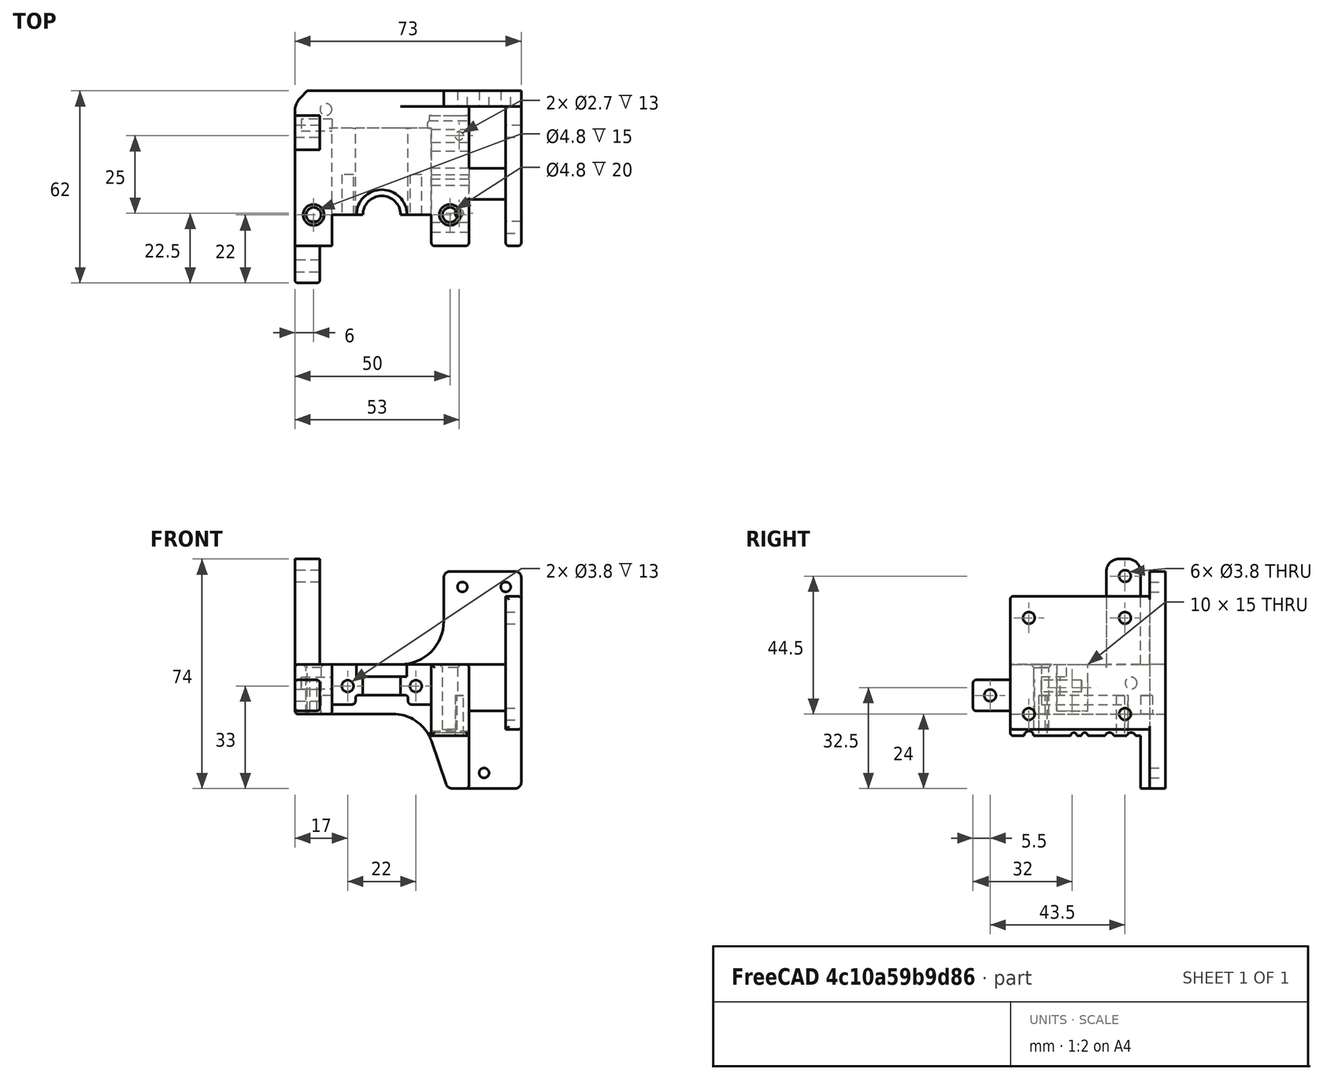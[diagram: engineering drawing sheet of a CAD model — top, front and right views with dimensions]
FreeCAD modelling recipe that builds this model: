
FCSTD DOCUMENT  (FreeCAD 0.19R)
Label: head7.1
License: All rights reserved
LicenseURL: http://en.wikipedia.org/wiki/All_rights_reserved
objects: Sketcher::SketchObject×22, PartDesign::Pocket×19, PartDesign::Fillet×15, PartDesign::Pad×3, PartDesign::Chamfer×2, PartDesign::Body×1, Mesh::Feature×1
note: 101 computed .brp shape members not serialized (recipe doc carries the construction recipe); baked Part::Feature solids carry a one-line shape summary decoded from their .brp

FEATURE [Sketcher::SketchObject] Sketch
  FullyConstrained = true
  MapMode = 5
  Support = -> [XY_Plane]
  sketch-geometry (5):
    g0: LineSegment StartX=0 StartY=0 StartZ=0 EndX=45 EndY=0 EndZ=0
    g1: LineSegment StartX=-28 StartY=0 StartZ=0 EndX=0 EndY=0 EndZ=0
    g2: LineSegment StartX=-28 StartY=0 StartZ=0 EndX=-28 EndY=-50 EndZ=0
    g3: LineSegment StartX=-28 StartY=-50 StartZ=0 EndX=45 EndY=-50 EndZ=0
    g4: LineSegment StartX=45 StartY=-50 StartZ=0 EndX=45 EndY=0 EndZ=0
  constraints (14):
    c: Coincident(g-1,g0)
    c: PointOnObject(g0,g-1)
    c: PointOnObject(g1,g-1)
    c: Coincident(g1,g0)
    c: Coincident(g1,g2)
    c: Vertical(g2)
    c: Coincident(g2,g3)
    c: Horizontal(g3)
    c: Coincident(g3,g4)
    c: Coincident(g4,g0)
    c: Vertical(g4)
    c: Distance(g4) = 50
    c: DistanceX(g0) = 45
    c: DistanceX(g1) = -28
FEATURE [PartDesign::Pad] Pad
  Direction = (1,1,1)
  Length = 70
  Length2 = 100
  Profile = -> Sketch
  Type = 0
FEATURE [Sketcher::SketchObject] Sketch001
  FullyConstrained = false
  MapMode = 5
  Placement = pos=(0,0,70) rot=(0,0,1;0rad)
  Support = -> [Pad]
  sketch-geometry (4):
    g0: LineSegment StartX=28.1122 StartY=-5 StartZ=0 EndX=40 EndY=-5 EndZ=0
    g1: LineSegment StartX=40 StartY=-5 StartZ=0 EndX=40 EndY=-51.78 EndZ=0
    g2: LineSegment StartX=40 StartY=-51.78 StartZ=0 EndX=28.1122 EndY=-51.78 EndZ=0
    g3: LineSegment StartX=28.1122 StartY=-51.78 StartZ=0 EndX=28.1122 EndY=-5 EndZ=0
  constraints (11):
    c: Coincident(g0,g1)
    c: Coincident(g1,g2)
    c: Coincident(g2,g3)
    c: Coincident(g3,g0)
    c: Horizontal(g0)
    c: Horizontal(g2)
    c: Vertical(g1)
    c: Vertical(g3)
    c: DistanceX(g0) = 40
    c: DistanceY(g1) = -51.78
    c: DistanceY(g0) = -5
FEATURE [PartDesign::Pocket] Pocket  label="BOBnotch"
  BaseFeature = -> Pad
  Length = 5
  Length2 = 100
  Profile = -> Sketch001
  Type = 1
FEATURE [Sketcher::SketchObject] Sketch002
  FullyConstrained = false
  MapMode = 5
  Placement = pos=(0,0,70) rot=(0,0,1;0rad)
  Support = -> [Pocket]
  sketch-geometry (6):
    g0: LineSegment StartX=30 StartY=-5 StartZ=0 EndX=30 EndY=-65.096 EndZ=0
    g1: LineSegment StartX=30 StartY=-65.096 StartZ=0 EndX=-40.7834 EndY=-65.096 EndZ=0
    g2: LineSegment StartX=-40.7834 StartY=-65.096 StartZ=0 EndX=-40.7834 EndY=12.9948 EndZ=0
    g3: LineSegment StartX=-40.7834 StartY=12.9948 StartZ=0 EndX=20 EndY=12.9948 EndZ=0
    g4: LineSegment StartX=20 StartY=12.9948 StartZ=0 EndX=20 EndY=-5 EndZ=0
    g5: LineSegment StartX=20 StartY=-5 StartZ=0 EndX=30 EndY=-5 EndZ=0
  constraints (15):
    c: Coincident(g0,g1)
    c: Coincident(g1,g2)
    c: Horizontal(g1)
    c: Vertical(g0)
    c: Vertical(g2)
    c: DistanceX(g0) = 30
    c: DistanceY(g0) = -5
    c: Coincident(g2,g3)
    c: Horizontal(g3)
    c: Coincident(g3,g4)
    c: Coincident(g4,g5)
    c: Coincident(g5,g0)
    c: Horizontal(g5)
    c: Vertical(g4)
    c: DistanceX(g3) = 20
FEATURE [PartDesign::Pocket] Pocket001  label="stepperplatform"
  BaseFeature = -> Pocket
  Length = 30
  Length2 = 100
  Profile = -> Sketch002
  Type = 0
FEATURE [Sketcher::SketchObject] Sketch003
  FullyConstrained = true
  MapMode = 5
  Placement = pos=(0,0,40) rot=(0,0,1;0rad)
  Support = -> [Pocket001]
  sketch-geometry (2):
    g0: Circle CenterX=-22 CenterY=-40 CenterZ=0 NormalX=0 NormalY=0 NormalZ=1 AngleXU=0 Radius=2.4
    g1: Circle CenterX=22 CenterY=-40 CenterZ=0 NormalX=0 NormalY=0 NormalZ=1 AngleXU=0 Radius=2.4
  constraints (5):
    c: Equal(g1,g0)
    c: Symmetric(g1,g0,g-2)
    c: Distance(g1,g0) = 44
    c: DistanceY(g0) = -40
    c: Diameter(g1) = 4.8
FEATURE [PartDesign::Pocket] Pocket002  label="steppermountholes"
  BaseFeature = -> Pocket001
  Length = 21
  Length2 = 100
  Profile = -> Sketch003
  Type = 0
FEATURE [Sketcher::SketchObject] Sketch004
  FullyConstrained = true
  MapMode = 5
  Placement = pos=(0,0,40) rot=(0,0,1;0rad)
  Support = -> [Pocket002]
  sketch-geometry (4):
    g0: ArcOfCircle CenterX=0 CenterY=-40 CenterZ=0 NormalX=0 NormalY=0 NormalZ=1 AngleXU=0 Radius=8.125 StartAngle=4e-16 EndAngle=3.14159
    g1: LineSegment StartX=8.125 StartY=-40 StartZ=0 EndX=8.125 EndY=-59.24 EndZ=0
    g2: LineSegment StartX=8.125 StartY=-59.24 StartZ=0 EndX=-8.125 EndY=-59.24 EndZ=0
    g3: LineSegment StartX=-8.125 StartY=-59.24 StartZ=0 EndX=-8.125 EndY=-40 EndZ=0
  constraints (11):
    c: PointOnObject(g0,g-2)
    c: Diameter(g0) = 16.25
    c: DistanceY(g0) = -40
    c: Coincident(g1,g2)
    c: Coincident(g2,g3)
    c: Horizontal(g2)
    c: Vertical(g3)
    c: Distance(g3) = 19.24
    c: Tangent(g3,g0) = 1.5708
    c: Tangent(g1,g0) = 1.5708
    c: Vertical(g1)
FEATURE [PartDesign::Pocket] Pocket003  label="hotendnotch001"
  BaseFeature = -> Pocket002
  Length = 4
  Length2 = 100
  Profile = -> Sketch004
  Type = 0
FEATURE [Sketcher::SketchObject] Sketch018
  FullyConstrained = true
  MapMode = 5
  Placement = pos=(0,0,36.5) rot=(0,0,1;0rad)
  sketch-geometry (4):
    g0: ArcOfCircle CenterX=0 CenterY=-40 CenterZ=0 NormalX=0 NormalY=0 NormalZ=1 AngleXU=0 Radius=6.1 StartAngle=-4e-14 EndAngle=3.14159
    g1: LineSegment StartX=6.1 StartY=-40 StartZ=0 EndX=6.1 EndY=-50 EndZ=0
    g2: LineSegment StartX=-6.1 StartY=-40 StartZ=0 EndX=-6.1 EndY=-50 EndZ=0
    g3: LineSegment StartX=6.1 StartY=-50 StartZ=0 EndX=-6.1 EndY=-50 EndZ=0
  constraints (11):
    c: PointOnObject(g0,g-2)
    c: Vertical(g1)
    c: Vertical(g2)
    c: Coincident(g3,g1)
    c: Coincident(g3,g2)
    c: Tangent(g1,g0) = 1.5708
    c: Tangent(g2,g0) = -1.5708
    c: DistanceY(g0) = -40
    c: Diameter(g0) = 12.2
    c: Horizontal(g3)
    c: Distance(g1) = 10
FEATURE [PartDesign::Pocket] Pocket004
  BaseFeature = -> Pocket003
  Length = 9
  Length2 = 100
  Profile = -> Sketch018
  Type = 0
FEATURE [Sketcher::SketchObject] Sketch021
  FullyConstrained = false
  MapMode = 5
  Placement = pos=(0,-50,0) rot=(1,0,0;1.5708rad)
  Support = -> [Pocket004]
  sketch-geometry (4):
    g0: LineSegment StartX=-16 StartY=43.4175 StartZ=0 EndX=16 EndY=43.4175 EndZ=0
    g1: LineSegment StartX=16 StartY=43.4175 StartZ=0 EndX=16 EndY=-9.74423 EndZ=0
    g2: LineSegment StartX=16 StartY=-9.74423 StartZ=0 EndX=-16 EndY=-9.74423 EndZ=0
    g3: LineSegment StartX=-16 StartY=-9.74423 StartZ=0 EndX=-16 EndY=43.4175 EndZ=0
  constraints (9):
    c: Coincident(g0,g1)
    c: Coincident(g1,g2)
    c: Coincident(g2,g3)
    c: Coincident(g3,g0)
    c: Horizontal(g2)
    c: Vertical(g1)
    c: Vertical(g3)
    c: Distance(g0,g0) = 32
    c: Symmetric(g0,g0,g-2)
FEATURE [PartDesign::Pocket] Pocket005  label="clampnotch"
  BaseFeature = -> Pocket004
  Length = 10
  Length2 = 100
  Profile = -> Sketch021
  Type = 0
FEATURE [Sketcher::SketchObject] Sketch022
  ExternalGeometry = -> [Pocket005]
  FullyConstrained = false
  MapMode = 5
  Placement = pos=(0,-50,0) rot=(1,0,0;1.5708rad)
  Support = -> [Pocket005]
  sketch-geometry (8):
    g0: LineSegment StartX=16 StartY=27.1 StartZ=0 EndX=16 EndY=-27.9602 EndZ=0
    g1: LineSegment StartX=16 StartY=-27.9602 StartZ=0 EndX=-16 EndY=-27.9602 EndZ=0
    g2: LineSegment StartX=-16 StartY=-27.9602 StartZ=0 EndX=-16 EndY=27.1 EndZ=0
    g3: LineSegment StartX=16 StartY=27.1 StartZ=0 EndX=8.5 EndY=27.1 EndZ=0
    g4: LineSegment StartX=8.5 StartY=27.1 StartZ=0 EndX=8.5 EndY=30.1 EndZ=0
    g5: LineSegment StartX=8.5 StartY=30.1 StartZ=0 EndX=-8.5 EndY=30.1 EndZ=0
    g6: LineSegment StartX=-8.5 StartY=30.1 StartZ=0 EndX=-8.5 EndY=27.1 EndZ=0
    g7: LineSegment StartX=-8.5 StartY=27.1 StartZ=0 EndX=-16 EndY=27.1 EndZ=0
  constraints (20):
    c: Coincident(g0,g1)
    c: Coincident(g1,g2)
    c: Horizontal(g1)
    c: Vertical(g0)
    c: Vertical(g2)
    c: Symmetric(g0,g2,g-2)
    c: Coincident(g0,g3)
    c: Horizontal(g3)
    c: Coincident(g3,g4)
    c: Coincident(g4,g5)
    c: Coincident(g5,g6)
    c: Vertical(g6)
    c: Coincident(g6,g7)
    c: Coincident(g7,g2)
    c: Symmetric(g4,g5,g-2)
    c: Symmetric(g3,g6,g-2)
    c: Distance(g-5,g5) = 5.9
    c: Distance(g4) = 3
    c: Distance(g0,g2) = 32
    c: Distance(g5) = 17
FEATURE [PartDesign::Pocket] Pocket006  label="fanNotch"
  BaseFeature = -> Pocket005
  Length = 38
  Length2 = 100
  Profile = -> Sketch022
  Type = 0
FEATURE [Sketcher::SketchObject] Sketch023
  ExternalGeometry = -> [Pocket006]
  FullyConstrained = true
  MapMode = 5
  Placement = pos=(0,-50,0) rot=(1,0,0;1.5708rad)
  Support = -> [Pocket006]
  sketch-geometry (4):
    g0: LineSegment StartX=-31.33 StartY=24 StartZ=0 EndX=13 EndY=24 EndZ=0
    g1: LineSegment StartX=13 StartY=24 StartZ=0 EndX=24 EndY=-8 EndZ=0
    g2: LineSegment StartX=24 StartY=-8 StartZ=0 EndX=-31.33 EndY=-8 EndZ=0
    g3: LineSegment StartX=-31.33 StartY=-8 StartZ=0 EndX=-31.33 EndY=24 EndZ=0
  constraints (12):
    c: Horizontal(g0)
    c: Coincident(g0,g1)
    c: Coincident(g1,g2)
    c: Horizontal(g2)
    c: Coincident(g2,g3)
    c: Coincident(g3,g0)
    c: DistanceX(g0) = 13
    c: DistanceX(g1) = 24
    c: DistanceY(g1) = -8
    c: Vertical(g3)
    c: Distance(g0) = 44.33
    c: Distance(g-3,g0) = 16
FEATURE [PartDesign::Pocket] Pocket007
  BaseFeature = -> Pocket006
  Length = 51
  Length2 = 100
  Profile = -> Sketch023
  Type = 0
FEATURE [Sketcher::SketchObject] Sketch008
  FullyConstrained = false
  MapMode = 5
  Placement = pos=(0,-50,0) rot=(1,0,0;1.5708rad)
  Support = -> [Pocket007]
  sketch-geometry (8):
    g0: LineSegment StartX=34.6158 StartY=72.6945 StartZ=0 EndX=53.669 EndY=72.6945 EndZ=0
    g1: LineSegment StartX=53.669 StartY=72.6945 StartZ=0 EndX=53.669 EndY=62 EndZ=0
    g2: LineSegment StartX=53.669 StartY=62 StartZ=0 EndX=34.6158 EndY=62 EndZ=0
    g3: LineSegment StartX=34.6158 StartY=62 StartZ=0 EndX=34.6158 EndY=72.6945 EndZ=0
    g4: LineSegment StartX=34.9227 StartY=19 StartZ=0 EndX=70.6727 EndY=19 EndZ=0
    g5: LineSegment StartX=70.6727 StartY=19 StartZ=0 EndX=70.6727 EndY=-17.1722 EndZ=0
    g6: LineSegment StartX=70.6727 StartY=-17.1722 StartZ=0 EndX=34.9227 EndY=-17.1722 EndZ=0
    g7: LineSegment StartX=34.9227 StartY=-17.1722 StartZ=0 EndX=34.9227 EndY=19 EndZ=0
  constraints (18):
    c: Coincident(g0,g1)
    c: Coincident(g1,g2)
    c: Coincident(g2,g3)
    c: Coincident(g3,g0)
    c: Horizontal(g0)
    c: Horizontal(g2)
    c: Vertical(g1)
    c: Vertical(g3)
    c: Coincident(g4,g5)
    c: Coincident(g5,g6)
    c: Coincident(g6,g7)
    c: Coincident(g7,g4)
    c: Horizontal(g4)
    c: Horizontal(g6)
    c: Vertical(g5)
    c: Vertical(g7)
    c: DistanceY(g2) = 62
    c: DistanceY(g4) = 19
FEATURE [PartDesign::Pocket] Pocket008
  BaseFeature = -> Pocket007
  Length = 45
  Length2 = 100
  Profile = -> Sketch008
  Type = 0
FEATURE [Sketcher::SketchObject] Sketch009
  FullyConstrained = true
  MapMode = 5
  Placement = pos=(45,0,0) rot=(0.57735,0.57735,0.57735;2.0944rad)
  Support = -> [Pocket008]
  sketch-geometry (5):
    g0: Circle CenterX=-44 CenterY=55 CenterZ=0 NormalX=0 NormalY=0 NormalZ=1 AngleXU=0 Radius=1.9
    g1: Circle CenterX=-13 CenterY=24 CenterZ=0 NormalX=0 NormalY=0 NormalZ=1 AngleXU=0 Radius=1.9
    g2: LineSegment StartX=-44 StartY=55 StartZ=0 EndX=-13 EndY=24 EndZ=0
    g3: Circle CenterX=-13 CenterY=55 CenterZ=0 NormalX=0 NormalY=0 NormalZ=1 AngleXU=0 Radius=1.9
    g4: Circle CenterX=-44 CenterY=24 CenterZ=0 NormalX=0 NormalY=0 NormalZ=1 AngleXU=0 Radius=1.9
  constraints (14):
    c: Coincident(g2,g0)
    c: Coincident(g2,g1)
    c: Angle(g2) = -0.785398
    c: DistanceX(g1) = -13
    c: DistanceY(g1) = 24
    c: Diameter(g4) = 3.8
    c: Equal(g4,g0)
    c: Equal(g4,g3)
    c: Equal(g4,g1)
    c: DistanceY(g4,g0) = 31
    c: DistanceX(g0,g3) = 31
    c: DistanceX(g4,g1) = 31
    c: DistanceY(g4) = 24
    c: DistanceY(g1,g3) = 31
FEATURE [PartDesign::Pocket] Pocket009  label="pcbholes"
  BaseFeature = -> Pocket008
  Length = 5
  Length2 = 100
  Profile = -> Sketch009
  Type = 0
FEATURE [Sketcher::SketchObject] Sketch015
  FullyConstrained = false
  MapMode = 5
  Placement = pos=(-28,0,0) rot=(0.57735,-0.57735,-0.57735;2.0944rad)
  Support = -> [Pocket009]
  sketch-geometry (8):
    g0: LineSegment StartX=8 StartY=74 StartZ=0 EndX=19 EndY=74 EndZ=0
    g1: LineSegment StartX=19 StartY=74 StartZ=0 EndX=19 EndY=35.8156 EndZ=0
    g2: LineSegment StartX=19 StartY=35.8156 StartZ=0 EndX=8 EndY=35.8156 EndZ=0
    g3: LineSegment StartX=8 StartY=35.8156 StartZ=0 EndX=8 EndY=74 EndZ=0
    g4: LineSegment StartX=42.1188 StartY=35 StartZ=0 EndX=62 EndY=35 EndZ=0
    g5: LineSegment StartX=62 StartY=35 StartZ=0 EndX=62 EndY=25 EndZ=0
    g6: LineSegment StartX=62 StartY=25 StartZ=0 EndX=42.1188 EndY=25 EndZ=0
    g7: LineSegment StartX=42.1188 StartY=25 StartZ=0 EndX=42.1188 EndY=35 EndZ=0
  constraints (22):
    c: Coincident(g0,g1)
    c: Coincident(g1,g2)
    c: Coincident(g2,g3)
    c: Coincident(g3,g0)
    c: Horizontal(g0)
    c: Horizontal(g2)
    c: Vertical(g1)
    c: Vertical(g3)
    c: DistanceY(g0) = 74
    c: Coincident(g4,g5)
    c: Coincident(g5,g6)
    c: Coincident(g6,g7)
    c: Coincident(g7,g4)
    c: Horizontal(g4)
    c: Horizontal(g6)
    c: Vertical(g5)
    c: Vertical(g7)
    c: DistanceX(g4) = 62
    c: DistanceY(g4) = 35
    c: DistanceY(g5) = 25
    c: DistanceX(g0) = 19
    c: DistanceX(g0) = 8
FEATURE [PartDesign::Pad] Pad001
  BaseFeature = -> Pocket009
  Direction = (1,1,1)
  Length = 8
  Length2 = 100
  Profile = -> Sketch015
  Reversed = true
  Type = 0
FEATURE [Sketcher::SketchObject] Sketch011
  FullyConstrained = true
  MapMode = 5
  Placement = pos=(-28,0,0) rot=(0.57735,-0.57735,-0.57735;2.0944rad)
  Support = -> [Pad001]
  sketch-geometry (3):
    g0: Circle CenterX=56.5 CenterY=30 CenterZ=0 NormalX=0 NormalY=0 NormalZ=1 AngleXU=0 Radius=1.9
    g1: Circle CenterX=13 CenterY=68.5 CenterZ=0 NormalX=0 NormalY=0 NormalZ=1 AngleXU=0 Radius=1.9
    g2: GeomPoint X=36 Y=48 Z=0
  constraints (8):
    c: Diameter(g0) = 3.8
    c: DistanceY(g0) = 30
    c: Diameter(g1) = 3.8
    c: DistanceX(g1) = 13
    c: DistanceY(g0,g2) = 18
    c: DistanceY(g2,g1) = 20.5
    c: DistanceX(g2,g0) = 20.5
    c: DistanceX(g1,g2) = 23
FEATURE [PartDesign::Pocket] Pocket010
  BaseFeature = -> Pad001
  Length = 10
  Length2 = 100
  Profile = -> Sketch011
  Type = 0
FEATURE [Sketcher::SketchObject] Sketch010
  FullyConstrained = true
  MapMode = 5
  Placement = pos=(0,0,0) rot=(0,0.707107,0.707107;3.14159rad)
  Support = -> [Pocket010]
  sketch-geometry (3):
    g0: Circle CenterX=-33 CenterY=5 CenterZ=0 NormalX=0 NormalY=0 NormalZ=1 AngleXU=0 Radius=1.6
    g1: Circle CenterX=-40 CenterY=65 CenterZ=0 NormalX=0 NormalY=0 NormalZ=1 AngleXU=0 Radius=1.6
    g2: Circle CenterX=-26 CenterY=65 CenterZ=0 NormalX=0 NormalY=0 NormalZ=1 AngleXU=0 Radius=1.6
  constraints (9):
    c: Diameter(g0) = 3.2
    c: Equal(g0,g2)
    c: Equal(g0,g1)
    c: DistanceX(g0) = -33
    c: Distance(g1,g2) = 14
    c: DistanceX(g2) = -26
    c: DistanceY(g0) = 5
    c: DistanceY(g2) = 65
    c: DistanceY(g1) = 65
FEATURE [PartDesign::Pocket] Pocket011
  BaseFeature = -> Pocket010
  Length = 7
  Length2 = 100
  Profile = -> Sketch010
  Type = 0
FEATURE [Sketcher::SketchObject] Sketch017
  FullyConstrained = false
  MapMode = 5
  Placement = pos=(-16,0,0) rot=(0.57735,0.57735,0.57735;2.0944rad)
  Support = -> [Pocket011]
  sketch-geometry (3):
    g0: Circle CenterX=26 CenterY=65 CenterZ=0 NormalX=0 NormalY=0 NormalZ=1 AngleXU=0 Radius=3
    g1: Circle CenterX=33 CenterY=5 CenterZ=0 NormalX=0 NormalY=0 NormalZ=1 AngleXU=0 Radius=3
    g2: Circle CenterX=40 CenterY=65 CenterZ=0 NormalX=0 NormalY=0 NormalZ=1 AngleXU=0 Radius=3
  constraints (3):
    c: Diameter(g2) = 6
    c: Equal(g2,g1)
    c: Equal(g2,g0)
FEATURE [PartDesign::Pocket] Pocket012
  BaseFeature = -> Pocket011
  Length = 2
  Length2 = 100
  Profile = -> Sketch017
  Type = 0
FEATURE [Sketcher::SketchObject] Sketch013
  ExternalGeometry = -> [Pocket012]
  FullyConstrained = true
  MapMode = 5
  Placement = pos=(-16,0,0) rot=(0.57735,0.57735,0.57735;2.0944rad)
  Support = -> [Pocket012]
  sketch-geometry (2):
    g0: Circle CenterX=-11 CenterY=34 CenterZ=0 NormalX=0 NormalY=0 NormalZ=1 AngleXU=0 Radius=1.9
    g1: Circle CenterX=11 CenterY=34 CenterZ=0 NormalX=0 NormalY=0 NormalZ=1 AngleXU=0 Radius=1.9
  constraints (5):
    c: Symmetric(g1,g0,g-2)
    c: Distance(g1,g0) = 22
    c: Diameter(g1) = 3.8
    c: Equal(g1,g0)
    c: Distance(g1,g-3) = 6
FEATURE [PartDesign::Pocket] Pocket013
  BaseFeature = -> Pocket012
  Length = 10
  Length2 = 100
  Profile = -> Sketch013
  Type = 0
FEATURE [Sketcher::SketchObject] Sketch014
  FullyConstrained = true
  MapMode = 5
  Placement = pos=(45,0,0) rot=(0.57735,0.57735,0.57735;2.0944rad)
  Support = -> [Pocket013]
  sketch-geometry (4):
    g0: LineSegment StartX=-35 StartY=40 StartZ=0 EndX=-25 EndY=40 EndZ=0
    g1: LineSegment StartX=-25 StartY=40 StartZ=0 EndX=-25 EndY=25 EndZ=0
    g2: LineSegment StartX=-25 StartY=25 StartZ=0 EndX=-35 EndY=25 EndZ=0
    g3: LineSegment StartX=-35 StartY=25 StartZ=0 EndX=-35 EndY=40 EndZ=0
  constraints (12):
    c: Coincident(g0,g1)
    c: Coincident(g1,g2)
    c: Coincident(g2,g3)
    c: Coincident(g3,g0)
    c: Horizontal(g0)
    c: Horizontal(g2)
    c: Vertical(g1)
    c: Vertical(g3)
    c: Distance(g1) = 15
    c: Distance(g0) = 10
    c: DistanceX(g0) = -25
    c: DistanceY(g1) = 25
FEATURE [PartDesign::Pad] Pad002  label="strut"
  BaseFeature = -> Pocket013
  Direction = (1,1,1)
  Length = 18
  Length2 = 100
  Profile = -> Sketch014
  Reversed = true
  Type = 0
FEATURE [Sketcher::SketchObject] Sketch025
  FullyConstrained = true
  MapMode = 5
  Placement = pos=(0,4.9e-15,22) rot=(1,0,0;3.14159rad)
  sketch-geometry (1):
    g0: Circle CenterX=-18 CenterY=6 CenterZ=0 NormalX=0 NormalY=0 NormalZ=1 AngleXU=0 Radius=1.9
  constraints (3):
    c: DistanceX(g0) = -18
    c: DistanceY(g0) = 6
    c: Diameter(g0) = 3.8
FEATURE [Sketcher::SketchObject] Sketch027
  ExternalGeometry = -> [Pad002]
  FullyConstrained = false
  MapMode = 5
  Placement = pos=(0,-50,0) rot=(1,0,0;1.5708rad)
  Support = -> [Pad002]
  sketch-geometry (4):
    g0: LineSegment StartX=9.59321 StartY=17 StartZ=0 EndX=31.7784 EndY=17 EndZ=0
    g1: LineSegment StartX=31.7784 StartY=17 StartZ=0 EndX=31.7784 EndY=-5.521 EndZ=0
    g2: LineSegment StartX=31.7784 StartY=-5.521 StartZ=0 EndX=9.59321 EndY=-5.521 EndZ=0
    g3: LineSegment StartX=9.59321 StartY=-5.521 StartZ=0 EndX=9.59321 EndY=17 EndZ=0
  constraints (9):
    c: Coincident(g0,g1)
    c: Coincident(g1,g2)
    c: Coincident(g2,g3)
    c: Coincident(g3,g0)
    c: Horizontal(g0)
    c: Horizontal(g2)
    c: Vertical(g1)
    c: Vertical(g3)
    c: Distance(g-3,g0) = 23
FEATURE [PartDesign::Pocket] Pocket014
  BaseFeature = -> Pad002
  Length = 42
  Length2 = 100
  Profile = -> Sketch027
  Type = 0
FEATURE [PartDesign::Pocket] Pocket015
  BaseFeature = -> Pocket014
  Length = 8
  Length2 = 100
  Profile = -> Sketch025
  Type = 0
FEATURE [Sketcher::SketchObject] Sketch028
  ExternalGeometry = -> [Pocket015]
  FullyConstrained = true
  MapMode = 5
  Placement = pos=(0,-40,5.3e-15) rot=(1,0,0;1.5708rad)
  Support = -> [Pocket015]
  sketch-geometry (2):
    g0: Circle CenterX=-11 CenterY=33 CenterZ=0 NormalX=0 NormalY=0 NormalZ=1 AngleXU=0 Radius=1.9
    g1: Circle CenterX=11 CenterY=33 CenterZ=0 NormalX=0 NormalY=0 NormalZ=1 AngleXU=0 Radius=1.9
  constraints (5):
    c: Diameter(g0) = 3.8
    c: Equal(g0,g1)
    c: Symmetric(g0,g1,g-2)
    c: Distance(g1,g-3) = 7
    c: Distance(g1,g0) = 22
FEATURE [PartDesign::Pocket] Pocket016
  BaseFeature = -> Pocket015
  Length = 13
  Length2 = 100
  Profile = -> Sketch028
  Type = 0
FEATURE [PartDesign::Fillet] Fillet
  Base = -> Pocket016 [Edge21]
  BaseFeature = -> Pocket016
  Radius = 13
  SupportTransform = false
FEATURE [PartDesign::Fillet] Fillet001
  Base = -> Fillet [Edge74]
  BaseFeature = -> Fillet
  Radius = 14
  SupportTransform = false
FEATURE [PartDesign::Chamfer] Chamfer
  Angle = 45
  Base = -> Fillet001 [Edge40]
  BaseFeature = -> Fillet001
  ChamferType = 0
  FlipDirection = false
  Size = 4
  Size2 = 1
  SupportTransform = false
FEATURE [PartDesign::Fillet] Fillet002
  Base = -> Chamfer [Edge30]
  BaseFeature = -> Chamfer
  Radius = 6
  SupportTransform = false
FEATURE [PartDesign::Fillet] Fillet003
  Base = -> Fillet002 [Edge145,Edge133]
  BaseFeature = -> Fillet002
  Radius = 2
  SupportTransform = false
FEATURE [PartDesign::Fillet] Fillet004
  Base = -> Fillet003 [Edge20,Edge33]
  BaseFeature = -> Fillet003
  Radius = 2
  SupportTransform = false
FEATURE [PartDesign::Fillet] Fillet005
  Base = -> Fillet004 [Edge227,Edge229,Edge230,Edge233]
  BaseFeature = -> Fillet004
  Radius = 1
  SupportTransform = false
FEATURE [PartDesign::Fillet] Fillet006
  Base = -> Fillet005 [Edge77]
  BaseFeature = -> Fillet005
  Radius = 1
  SupportTransform = false
FEATURE [PartDesign::Fillet] Fillet007
  Base = -> Fillet006 [Edge179,Edge172,Edge176,Edge175]
  BaseFeature = -> Fillet006
  Radius = 1
  SupportTransform = false
FEATURE [Sketcher::SketchObject] Sketch030
  FullyConstrained = false
  MapMode = 5
  Placement = pos=(45,0,0) rot=(0.57735,0.57735,0.57735;2.0944rad)
  Support = -> [Fillet007]
  sketch-geometry (5):
    g0: Circle CenterX=-11 CenterY=16.5 CenterZ=0 NormalX=0 NormalY=0 NormalZ=1 AngleXU=0 Radius=1.5
    g1: Circle CenterX=-18 CenterY=16.5 CenterZ=0 NormalX=0 NormalY=0 NormalZ=1 AngleXU=0 Radius=1.5
    g2: Circle CenterX=-44 CenterY=17 CenterZ=0 NormalX=0 NormalY=0 NormalZ=1 AngleXU=0 Radius=1.5
    g3: Circle CenterX=-29.5 CenterY=17 CenterZ=0 NormalX=0 NormalY=0 NormalZ=1 AngleXU=0 Radius=1
    g4: Circle CenterX=-26 CenterY=17 CenterZ=0 NormalX=0 NormalY=0 NormalZ=1 AngleXU=0 Radius=1
  constraints (14):
    c: Equal(g0,g1)
    c: Equal(g0,g2)
    c: Equal(g4,g3)
    c: Distance(g4,g3) = 3.5
    c: DistanceX(g1,g0) = 7
    c: DistanceX(g4,g0) = 15
    c: DistanceX(g2,g0) = 33
    c: DistanceY(g0) = 16.5
    c: DistanceY(g1) = 16.5
    c: DistanceY(g2) = 17
    c: DistanceY(g4) = 17
    c: DistanceY(g3) = 17
    c: Diameter(g0) = 3
    c: Diameter(g4) = 2
FEATURE [PartDesign::Pocket] Pocket017
  BaseFeature = -> Fillet007
  Length = 5
  Length2 = 100
  Profile = -> Sketch030
  Type = 1
FEATURE [Sketcher::SketchObject] Sketch029
  FullyConstrained = true
  MapMode = 5
  Placement = pos=(0,3.8e-15,17) rot=(1,0,0;3.14159rad)
  Support = -> [Pocket017]
  sketch-geometry (2):
    g0: Circle CenterX=25 CenterY=39.5 CenterZ=0 NormalX=0 NormalY=0 NormalZ=1 AngleXU=0 Radius=1.35
    g1: Circle CenterX=25 CenterY=14.5 CenterZ=0 NormalX=0 NormalY=0 NormalZ=1 AngleXU=0 Radius=1.35
  constraints (6):
    c: Diameter(g1) = 2.7
    c: Equal(g1,g0)
    c: DistanceX(g0) = 25
    c: DistanceX(g1) = 25
    c: DistanceY(g0) = 39.5
    c: DistanceY(g1) = 14.5
FEATURE [PartDesign::Pocket] Pocket018
  BaseFeature = -> Pocket017
  Length = 13
  Length2 = 100
  Profile = -> Sketch029
  Type = 0
FEATURE [PartDesign::Fillet] Fillet008
  Base = -> Pocket018 [Edge118,Edge215,Edge217,Edge32]
  BaseFeature = -> Pocket018
  Radius = 1
  SupportTransform = false
FEATURE [PartDesign::Fillet] Fillet009
  Base = -> Fillet008 [Edge132,Edge110]
  BaseFeature = -> Fillet008
  Radius = 4
  SupportTransform = false
FEATURE [PartDesign::Chamfer] Chamfer001
  Angle = 45
  Base = -> Fillet009 [Edge37,Edge36]
  BaseFeature = -> Fillet009
  ChamferType = 0
  FlipDirection = false
  Size = 1
  Size2 = 1
  SupportTransform = false
FEATURE [PartDesign::Fillet] Fillet010
  Base = -> Chamfer001 [Face3]
  BaseFeature = -> Chamfer001
  Radius = 1
  SupportTransform = false
FEATURE [PartDesign::Fillet] Fillet011
  Base = -> Fillet010 [Face104]
  BaseFeature = -> Fillet010
  Radius = 1
  SupportTransform = false
FEATURE [PartDesign::Fillet] Fillet012
  Base = -> Fillet011 [Edge60]
  BaseFeature = -> Fillet011
  Radius = 1
  SupportTransform = false
FEATURE [PartDesign::Fillet] Fillet013
  Base = -> Fillet012 [Edge21]
  BaseFeature = -> Fillet012
  Radius = 1
  SupportTransform = false
FEATURE [PartDesign::Fillet] Fillet014
  Base = -> Fillet013 [Face117]
  BaseFeature = -> Fillet013
  Radius = 1
  SupportTransform = false
FEATURE [PartDesign::Body] Body
  Group = -> [Sketch,Pad,Sketch001,Pocket,Sketch002,Pocket001,Sketch003,Pocket002,Sketch004,Pocket003,Sketch008,Sketch009,Sketch010,Sketch011,Sketch013,Sketch014,Sketch015,Sketch017,Sketch018,Pocket004,Sketch021,Pocket005,Sketch022,Pocket006,Sketch023,Pocket007,Pocket008,Pocket009,Pad001,Pocket010,Pocket011,Pocket012,Pocket013,Pad002,Sketch025,Sketch027,Pocket014,Pocket015,Sketch028,Pocket016,Fillet,Fillet001,+19 more]
  Origin = -> Origin
  Tip = -> Fillet014
FEATURE [Mesh::Feature] Mesh  label="Fillet014 (Meshed)"
